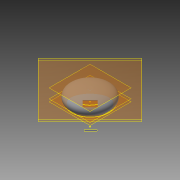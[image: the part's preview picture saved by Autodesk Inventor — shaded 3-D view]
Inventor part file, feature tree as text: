
AUTODESK INVENTOR PART (.ipt)
format: ipt  version: 2014 (Build 180170000, 170)  size: 190,976 bytes
history: native  units: mm
features: sketch x8, reference x8, plane x6, extrude x2, loft x1, projected_geometry x1, other x1
ambient origin geometry x8: Origin, YZ Plane, XZ Plane, XY Plane, X Axis, Y Axis, Z Axis, Center Point
bodies: Solid1 (feature_tree)
feature tree (27):
  plane  "Work Plane1"
  sketch  "Sketch2"  dims[d0=20.0mm d1=150.0mm]
  plane  "Work Plane2"
  sketch  "Sketch3"  dims[d2=0.0mm d3=90.0deg d4=0.0mm d5=90.0deg]
  plane  "Work Plane3"
  loft  "Loft1"
  extrude  "Extrusion1"  TaperAngle=0.0deg  [1 undecoded]
  sketch  "Sketch6"  dims[d11=22.68928mm d12=84.5mm]
  plane  "Work Plane4"
  sketch  "Sketch7"  dims[d13=40.0mm]
  sketch  "Sketch8"  dims[d14=20.0mm]
  plane  "Work Plane6"
  extrude  "Extrusion2"  Depth=115.0mm
  sketch  "Sketch4"  dims[d6=0.0mm d7=90.0deg d8=115.0mm]
  sketch  "Sketch5"  dims[d9=30.0mm d10=0.0mm]
  reference  "Reference2"
  reference  "Reference3"
  reference  "Reference4"
  reference  "Reference5"
  reference  "Reference6"
  reference  "Reference7"
  projected_geometry  "Projected Loop1"
  reference  "Reference8"
  reference  "Reference9"
  other  "Work Axis1"
  plane  "Work Plane5"
  sketch  "Sketch9"  dims[d15=81.25mm d16=0.0mm]
note: 1 required parameter value undecoded (feature->parameter linkage not recoverable at this tier; creation-order binding heuristic only, values carry confidence <= 0.55)
